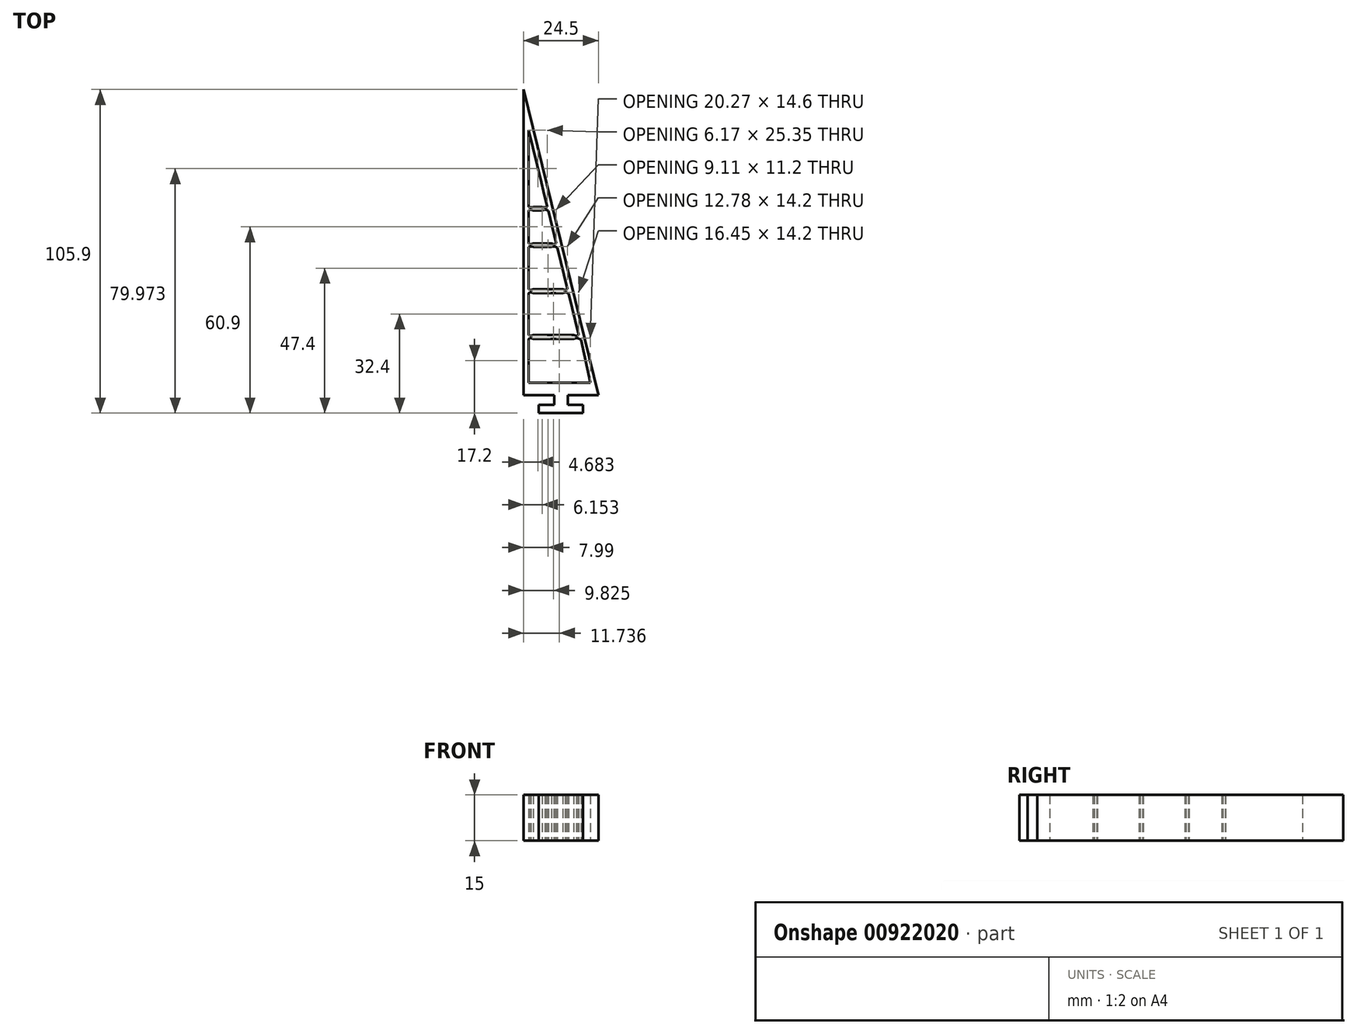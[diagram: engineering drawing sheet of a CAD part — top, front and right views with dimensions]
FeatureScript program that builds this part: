
annotation { "Feature Type Name" : "Feature", "Feature Type Description" : "" }
export const myFeature = defineFeature(function(context is Context, id is Id, definition is map)
    precondition{}
    {
        {
            var Q0;
            Q0=qCreatedBy(makeId("Top.planeOp"),FACE);
            var sketch = newSketch(context, id + "F0", { "sketchPlane" : qUnion([Q0])});
            skLineSegment(sketch, "E0", {"start": v(0, 0) * mm, "end": v(14.5, 0) * mm});
            skLineSegment(sketch, "E1", {"start": v(14.5, 0) * mm, "end": v(14.5, 2.7) * mm});
            skLineSegment(sketch, "E2", {"start": v(14.5, 2.7) * mm, "end": v(9.5, 2.7) * mm});
            skLineSegment(sketch, "E3", {"start": v(0, 0) * mm, "end": v(0, 2.7) * mm});
            skLineSegment(sketch, "E4", {"start": v(0, 2.7) * mm, "end": v(5, 2.7) * mm});
            skLineSegment(sketch, "E5", {"start": v(5, 2.7) * mm, "end": v(5, 5.9) * mm});
            skLineSegment(sketch, "E6", {"start": v(9.5, 2.7) * mm, "end": v(9.5, 5.9) * mm});
            skLineSegment(sketch, "E7", {"start": v(9.5, 5.9) * mm, "end": v(19.5, 5.9) * mm});
            skLineSegment(sketch, "E8", {"start": v(5, 5.9) * mm, "end": v(-5, 5.9) * mm});
            skLineSegment(sketch, "E9", {"start": v(-5, 5.9) * mm, "end": v(-5, 105.9) * mm});
            skLineSegment(sketch, "E10", {"start": v(-5, 105.9) * mm, "end": v(19.5, 5.9) * mm});
            skLineSegment(sketch, "E11.0", {"start": v(-3.4, 9.9) * mm, "end": v(-3.4, 23.07) * mm});
            skLineSegment(sketch, "E12.0", {"start": v(-3.4, 92.65) * mm, "end": v(0.8, 75.49) * mm});
            skLineSegment(sketch, "E13", {"start": v(16.87, 9.9) * mm, "end": v(-3.4, 9.9) * mm});
            skLineSegment(sketch, "E14", {"start": v(-3.4, 24.9) * mm, "end": v(13.2, 24.9) * mm, "construction": true});
            skLineSegment(sketch, "E15", {"start": v(-3.4, 39.9) * mm, "end": v(9.52, 39.9) * mm, "construction": true});
            skLineSegment(sketch, "E16", {"start": v(-3.4, 54.9) * mm, "end": v(5.85, 54.9) * mm, "construction": true});
            skLineSegment(sketch, "E17", {"start": v(-3.4, 66.9) * mm, "end": v(2.9, 66.9) * mm, "construction": true});
            skLineSegment(sketch, "E18", {"start": v(-3.4, 76.9) * mm, "end": v(0.46, 76.9) * mm, "construction": true});
            skLineSegment(sketch, "E19.trimOffspring", {"start": v(-3.4, 75.38) * mm, "end": v(-3.4, 92.65) * mm});
            skLineSegment(sketch, "E20.trimOffspring", {"start": v(1.52, 72.6) * mm, "end": v(2.77, 67.5) * mm});
            skLineSegment(sketch, "E21.trimOffspring", {"start": v(-3.4, 67.5) * mm, "end": v(-3.4, 72.42) * mm});
            skLineSegment(sketch, "E22.trimOffspring", {"start": v(3.1, 66.13) * mm, "end": v(5.7, 55.5) * mm});
            skLineSegment(sketch, "E23.trimOffspring", {"start": v(-3.4, 55.5) * mm, "end": v(-3.4, 66.3) * mm});
            skLineSegment(sketch, "E24.trimOffspring", {"start": v(6.04, 54.13) * mm, "end": v(9.38, 40.5) * mm});
            skLineSegment(sketch, "E25.trimOffspring", {"start": v(9.7, 39.14) * mm, "end": v(13.05, 25.5) * mm});
            skLineSegment(sketch, "E26.trimOffspring", {"start": v(13.75, 23.95) * mm, "end": v(16.87, 9.9) * mm});
            skLineSegment(sketch, "E27.trimOffspring", {"start": v(-3.4, 26.73) * mm, "end": v(-3.4, 39.3) * mm});
            skLineSegment(sketch, "E28.trimOffspring", {"start": v(-3.4, 40.47) * mm, "end": v(-3.4, 54.3) * mm});
            skLineSegment(sketch, "E29", {"start": v(-3.4, 75.38) * mm, "end": v(-3.4, 72.42) * mm});
            skLineSegment(sketch, "E30", {"start": v(0.8, 75.49) * mm, "end": v(1.52, 72.6) * mm});
            skLineSegment(sketch, "E31", {"start": v(-1.8, 25.5) * mm, "end": v(11.45, 25.5) * mm});
            skLineSegment(sketch, "E32", {"start": v(-1.8, 24.3) * mm, "end": v(11.45, 24.3) * mm});
            skLineSegment(sketch, "E33", {"start": v(-3, 25.3) * mm, "end": v(-2.6, 25.3) * mm});
            skLineSegment(sketch, "E34", {"start": v(-2.6, 25.3) * mm, "end": v(-1.8, 25.5) * mm});
            skLineSegment(sketch, "E35", {"start": v(-3, 25.3) * mm, "end": v(-3.4, 25.5) * mm});
            skLineSegment(sketch, "E36", {"start": v(-3.4, 26.73) * mm, "end": v(-3.4, 25.5) * mm});
            skLineSegment(sketch, "E37.MirrorCS", {"start": v(-3, 24.5) * mm, "end": v(-2.6, 24.5) * mm});
            skLineSegment(sketch, "E38.MirrorCS", {"start": v(-3, 24.5) * mm, "end": v(-3.4, 24.3) * mm});
            skLineSegment(sketch, "E39.MirrorCS", {"start": v(-2.6, 24.5) * mm, "end": v(-1.8, 24.3) * mm});
            skLineSegment(sketch, "E40", {"start": v(-3.4, 24.3) * mm, "end": v(-3.4, 23.07) * mm});
            skLineSegment(sketch, "E41", {"start": v(11.45, 25.5) * mm, "end": v(12.25, 25.3) * mm});
            skLineSegment(sketch, "E42", {"start": v(12.25, 25.3) * mm, "end": v(12.65, 25.3) * mm});
            skLineSegment(sketch, "E43", {"start": v(12.65, 25.3) * mm, "end": v(13.05, 25.5) * mm});
            skPoint(sketch, "E44.orphan", {"position": v(13.03, 25.5) * mm});
            skLineSegment(sketch, "E45.MirrorCS", {"start": v(12.65, 24.5) * mm, "end": v(13.75, 23.95) * mm});
            skLineSegment(sketch, "E46.MirrorCS", {"start": v(11.45, 24.3) * mm, "end": v(12.25, 24.5) * mm});
            skLineSegment(sketch, "E47.MirrorCS", {"start": v(12.25, 24.5) * mm, "end": v(12.65, 24.5) * mm});
            skPoint(sketch, "E48.orphan", {"position": v(13.05, 24.3) * mm});
            skLineSegment(sketch, "E49", {"start": v(-3, 40.3) * mm, "end": v(-2.6, 40.3) * mm});
            skLineSegment(sketch, "E50", {"start": v(-2.6, 40.3) * mm, "end": v(-1.8, 40.5) * mm});
            skLineSegment(sketch, "E51", {"start": v(-3, 40.3) * mm, "end": v(-3.4, 40.47) * mm});
            skLineSegment(sketch, "E52.MirrorCS", {"start": v(-3, 39.5) * mm, "end": v(-2.6, 39.5) * mm});
            skLineSegment(sketch, "E53.MirrorCS", {"start": v(-3, 39.5) * mm, "end": v(-3.4, 39.3) * mm});
            skLineSegment(sketch, "E54.MirrorCS", {"start": v(-2.6, 39.5) * mm, "end": v(-1.8, 39.3) * mm});
            skPoint(sketch, "E55.orphan", {"position": v(-3.4, 38.07) * mm});
            skPoint(sketch, "E56.orphan", {"position": v(-3.4, 40.47) * mm});
            skLineSegment(sketch, "E57", {"start": v(-1.8, 39.3) * mm, "end": v(7.78, 39.3) * mm});
            skLineSegment(sketch, "E58", {"start": v(-1.8, 40.5) * mm, "end": v(7.78, 40.5) * mm});
            skLineSegment(sketch, "E59", {"start": v(7.78, 40.5) * mm, "end": v(8.58, 40.3) * mm});
            skLineSegment(sketch, "E60", {"start": v(8.58, 40.3) * mm, "end": v(8.98, 40.3) * mm});
            skLineSegment(sketch, "E61", {"start": v(8.98, 40.3) * mm, "end": v(9.38, 40.5) * mm});
            skLineSegment(sketch, "E62.MirrorCS", {"start": v(8.98, 39.5) * mm, "end": v(9.7, 39.14) * mm});
            skLineSegment(sketch, "E63.MirrorCS", {"start": v(7.78, 39.3) * mm, "end": v(8.58, 39.5) * mm});
            skLineSegment(sketch, "E64.MirrorCS", {"start": v(8.58, 39.5) * mm, "end": v(8.98, 39.5) * mm});
            skPoint(sketch, "E65.orphan", {"position": v(9.38, 39.3) * mm});
            skLineSegment(sketch, "E66", {"start": v(-3.4, 55.5) * mm, "end": v(-3, 55.3) * mm});
            skLineSegment(sketch, "E67", {"start": v(-3, 55.3) * mm, "end": v(-2.6, 55.3) * mm});
            skLineSegment(sketch, "E68", {"start": v(-2.6, 55.3) * mm, "end": v(-1.8, 55.5) * mm});
            skLineSegment(sketch, "E69", {"start": v(-1.8, 55.5) * mm, "end": v(4.1, 55.5) * mm});
            skLineSegment(sketch, "E70", {"start": v(4.1, 55.5) * mm, "end": v(4.9, 55.3) * mm});
            skLineSegment(sketch, "E71", {"start": v(4.9, 55.3) * mm, "end": v(5.3, 55.3) * mm});
            skLineSegment(sketch, "E72", {"start": v(5.3, 55.3) * mm, "end": v(5.7, 55.5) * mm});
            skPoint(sketch, "E73.orphan", {"position": v(-3.4, 56.73) * mm});
            skLineSegment(sketch, "E74.MirrorCS", {"start": v(5.3, 54.5) * mm, "end": v(6.04, 54.13) * mm});
            skLineSegment(sketch, "E75.MirrorCS", {"start": v(4.9, 54.5) * mm, "end": v(5.3, 54.5) * mm});
            skLineSegment(sketch, "E76.MirrorCS", {"start": v(4.1, 54.3) * mm, "end": v(4.9, 54.5) * mm});
            skLineSegment(sketch, "E77.MirrorCS", {"start": v(-1.8, 54.3) * mm, "end": v(4.1, 54.3) * mm});
            skLineSegment(sketch, "E78.MirrorCS", {"start": v(-2.6, 54.5) * mm, "end": v(-1.8, 54.3) * mm});
            skLineSegment(sketch, "E79.MirrorCS", {"start": v(-3.4, 54.3) * mm, "end": v(-3, 54.5) * mm});
            skLineSegment(sketch, "E80.MirrorCS", {"start": v(-3, 54.5) * mm, "end": v(-2.6, 54.5) * mm});
            skPoint(sketch, "E81.orphan", {"position": v(5.7, 54.3) * mm});
            skLineSegment(sketch, "E82", {"start": v(-3.4, 67.5) * mm, "end": v(-3, 67.3) * mm});
            skLineSegment(sketch, "E83", {"start": v(-3, 67.3) * mm, "end": v(-2.6, 67.3) * mm});
            skLineSegment(sketch, "E84", {"start": v(-2.6, 67.3) * mm, "end": v(-1.8, 67.5) * mm});
            skLineSegment(sketch, "E85", {"start": v(-1.8, 67.5) * mm, "end": v(1.17, 67.5) * mm});
            skLineSegment(sketch, "E86", {"start": v(1.17, 67.5) * mm, "end": v(1.97, 67.3) * mm});
            skLineSegment(sketch, "E87", {"start": v(1.97, 67.3) * mm, "end": v(2.37, 67.3) * mm});
            skLineSegment(sketch, "E88", {"start": v(2.37, 67.3) * mm, "end": v(2.77, 67.5) * mm});
            skPoint(sketch, "E89.orphan", {"position": v(-3.4, 68.73) * mm});
            skLineSegment(sketch, "E90.MirrorCS", {"start": v(2.37, 66.5) * mm, "end": v(3.1, 66.13) * mm});
            skLineSegment(sketch, "E91.MirrorCS", {"start": v(1.97, 66.5) * mm, "end": v(2.37, 66.5) * mm});
            skLineSegment(sketch, "E92.MirrorCS", {"start": v(1.17, 66.3) * mm, "end": v(1.97, 66.5) * mm});
            skLineSegment(sketch, "E93.MirrorCS", {"start": v(-1.8, 66.3) * mm, "end": v(1.17, 66.3) * mm});
            skLineSegment(sketch, "E94.MirrorCS", {"start": v(-2.6, 66.5) * mm, "end": v(-1.8, 66.3) * mm});
            skLineSegment(sketch, "E95.MirrorCS", {"start": v(-3.4, 66.3) * mm, "end": v(-3, 66.5) * mm});
            skLineSegment(sketch, "E96.MirrorCS", {"start": v(-3, 66.5) * mm, "end": v(-2.6, 66.5) * mm});
            skPoint(sketch, "E97.orphan", {"position": v(2.77, 66.3) * mm});
            skSolve(sketch);
        }
        {
            var Q0;
            Q0=qSketchRegion(id+"F0",true);
            extrude(context, id + "F1", {"entities" : qUnion([Q0]), "depth" : 15 * mm, "offsetDistance" : 25 * mm});
        }
    });
